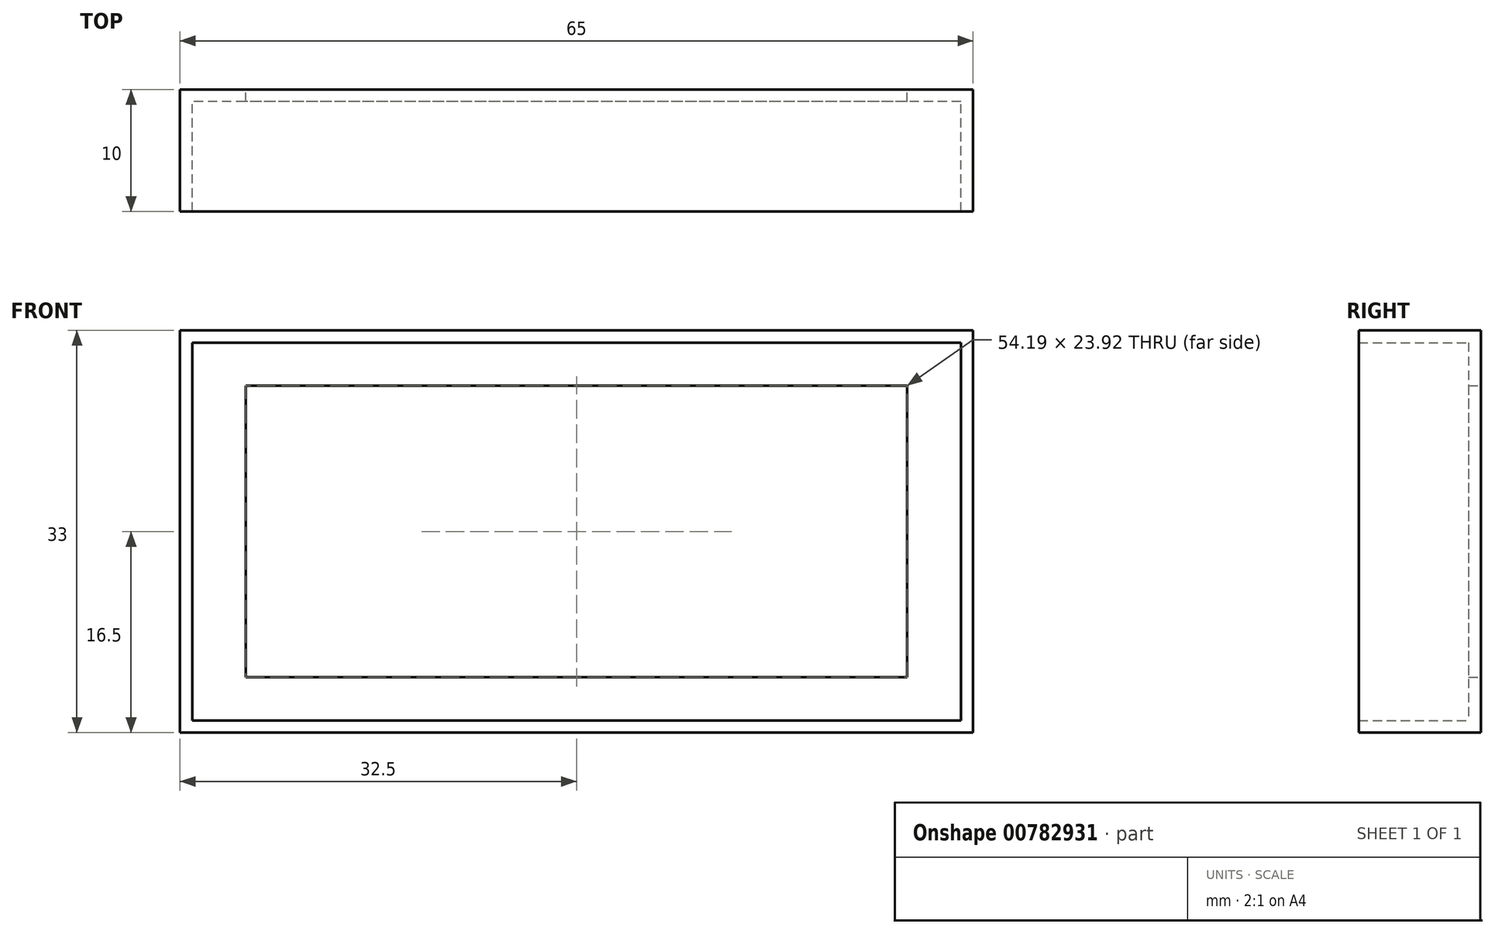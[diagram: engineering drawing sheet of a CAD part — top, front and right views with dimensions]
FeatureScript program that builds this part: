
annotation { "Feature Type Name" : "Feature", "Feature Type Description" : "" }
export const myFeature = defineFeature(function(context is Context, id is Id, definition is map)
    precondition{}
    {
        {
            var Q0;
            Q0=qCreatedBy(makeId("Front.planeOp"),FACE);
            var sketch = newSketch(context, id + "F0", { "sketchPlane" : qUnion([Q0])});
            skLineSegment(sketch, "E0.bottom", {"start": v(0, 0) * mm, "end": v(0, 0) * mm});
            skLineSegment(sketch, "E0.top", {"start": v(0, 0) * mm, "end": v(0, 0) * mm});
            skLineSegment(sketch, "E0.left", {"start": v(0, 0) * mm, "end": v(0, 0) * mm});
            skLineSegment(sketch, "E0.right", {"start": v(0, 0) * mm, "end": v(0, 0) * mm});
            skPoint(sketch, "E0.middle", {"position": v(0, 0) * mm});
            skLineSegment(sketch, "E1.bottom", {"start": v(48.15, -25.9) * mm, "end": v(-48.15, -25.9) * mm});
            skLineSegment(sketch, "E1.top", {"start": v(48.15, 25.9) * mm, "end": v(-48.15, 25.9) * mm});
            skLineSegment(sketch, "E1.left", {"start": v(48.15, -25.9) * mm, "end": v(48.15, 25.9) * mm});
            skLineSegment(sketch, "E1.right", {"start": v(-48.15, -25.9) * mm, "end": v(-48.15, 25.9) * mm});
            skLineSegment(sketch, "E2.bottom", {"start": v(32.5, 16.5) * mm, "end": v(-32.5, 16.5) * mm});
            skLineSegment(sketch, "E2.top", {"start": v(32.5, -16.5) * mm, "end": v(-32.5, -16.5) * mm});
            skLineSegment(sketch, "E2.left", {"start": v(32.5, 16.5) * mm, "end": v(32.5, -16.5) * mm});
            skLineSegment(sketch, "E2.right", {"start": v(-32.5, 16.5) * mm, "end": v(-32.5, -16.5) * mm});
            skLineSegment(sketch, "E3.bottom", {"start": v(-27.1, -11.96) * mm, "end": v(27.1, -11.96) * mm});
            skLineSegment(sketch, "E3.top", {"start": v(-27.1, 11.96) * mm, "end": v(27.1, 11.96) * mm});
            skLineSegment(sketch, "E3.left", {"start": v(-27.1, -11.96) * mm, "end": v(-27.1, 11.96) * mm});
            skLineSegment(sketch, "E3.right", {"start": v(27.1, -11.96) * mm, "end": v(27.1, 11.96) * mm});
            skSolve(sketch);
        }
        {
            var Q0;
            Q0=makeQuery(id+"F0.imprint","IMPRINT",FACE,{"disambiguationData":[TD([[makeQuery(id+"F0.imprint","IMPRINT",EDGE,{"derivedFrom":sQuery(id+"F0.wireOp",EDGE,"E2.bottom")}),1.0]])]});
            var Q1;
            Q1=makeQuery(id+"F0.imprint","IMPRINT",FACE,{"disambiguationData":[TD([[makeQuery(id+"F0.imprint","IMPRINT",EDGE,{"derivedFrom":sQuery(id+"F0.wireOp",EDGE,"E3.bottom")}),1.0]])]});
            extrude(context, id + "F1", {"entities" : qUnion([Q0, Q1]), "depth" : 10 * mm, "offsetDistance" : 25 * mm});
        }
        {
            var Q0;
            Q0=makeQuery(id+"F1.opExtrude","CAP_FACE",FACE,{"disambiguationData":[OSD([sQuery(id+"F0.wireOp",EDGE,"E2.bottom"),sQuery(id+"F0.wireOp",EDGE,"E2.top"),sQuery(id+"F0.wireOp",EDGE,"E2.left"),sQuery(id+"F0.wireOp",EDGE,"E2.right")])],"isStart":false});
            shell(context, id + "F2", {"entities" : qUnion([Q0]), "thickness" : 1 * mm});
        }
        {
            var Q0;
            Q0=makeQuery(id+"F0.imprint","IMPRINT",FACE,{"disambiguationData":[TD([[makeQuery(id+"F0.imprint","IMPRINT",EDGE,{"derivedFrom":sQuery(id+"F0.wireOp",EDGE,"E3.bottom")}),1.0]])]});
            extrude(context, id + "F3", {"entities" : qUnion([Q0]), "operationType" : NewBodyOperationType.REMOVE, "depth" : 73.8 * mm, "offsetDistance" : 25 * mm});
        }
    });
